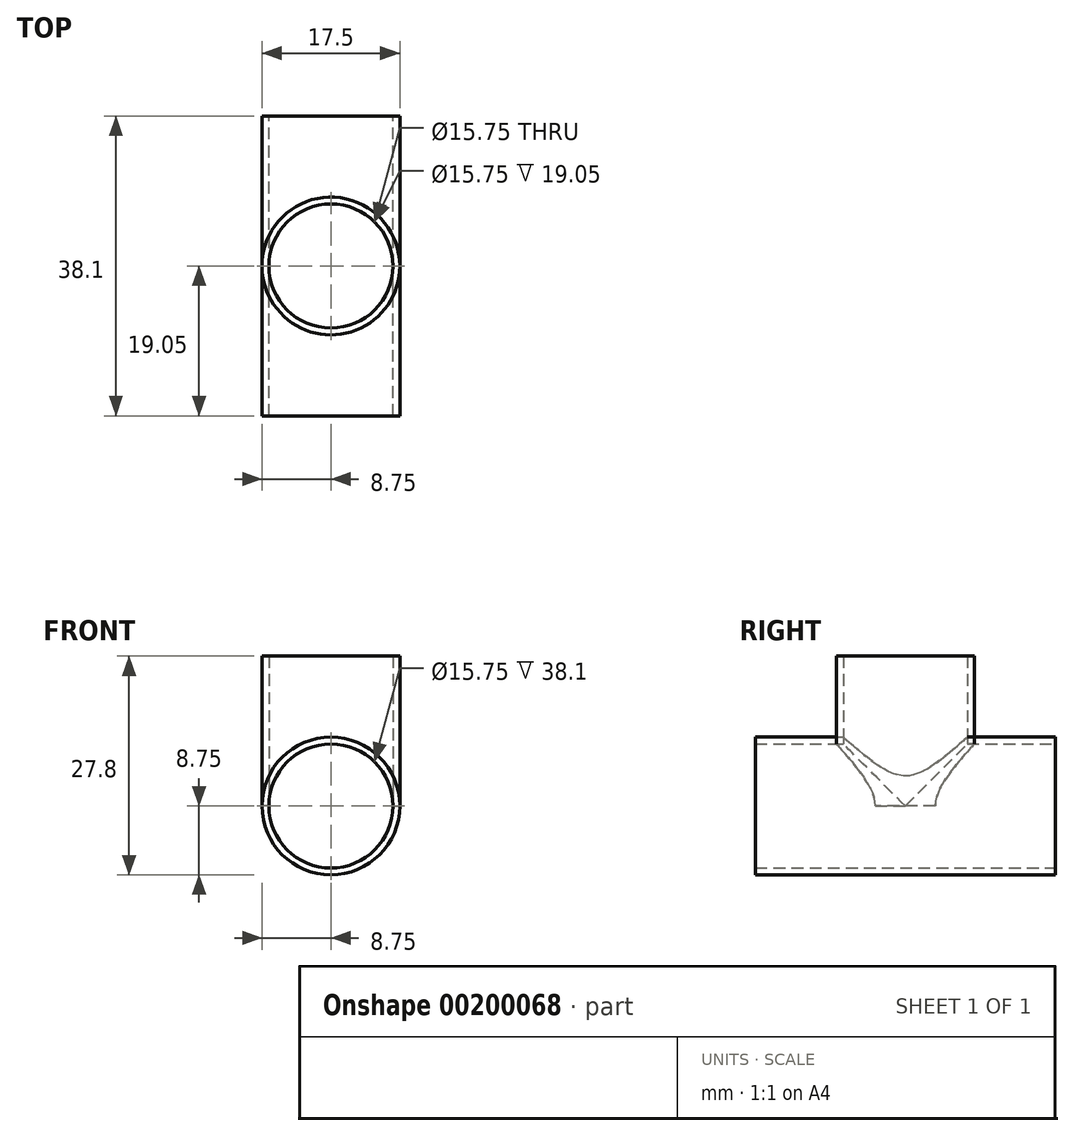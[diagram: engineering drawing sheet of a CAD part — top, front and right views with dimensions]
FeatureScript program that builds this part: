
annotation { "Feature Type Name" : "Feature", "Feature Type Description" : "" }
export const myFeature = defineFeature(function(context is Context, id is Id, definition is map)
    precondition{}
    {
        {
            var Q0;
            Q0=qCreatedBy(makeId("Front.planeOp"),FACE);
            var sketch = newSketch(context, id + "F0", { "sketchPlane" : qUnion([Q0])});
            skCircle(sketch, "E0", {"center": v(0, 0) * mm, "radius": 7.87 * mm});
            skCircle(sketch, "E1", {"center": v(0, 0) * mm, "radius": 8.75 * mm});
            skSolve(sketch);
        }
        {
            var Q0;
            Q0=qCreatedBy(makeId("Top.planeOp"),FACE);
            var sketch = newSketch(context, id + "F1", { "sketchPlane" : qUnion([Q0])});
            skCircle(sketch, "E2", {"center": v(0, 0) * mm, "radius": 8.75 * mm});
            skCircle(sketch, "E3", {"center": v(0, 0) * mm, "radius": 7.87 * mm});
            skSolve(sketch);
        }
        {
            var Q0;
            Q0=makeQuery(id+"F0.imprint","IMPRINT",FACE,{"disambiguationData":[TD([[makeQuery(id+"F0.imprint","IMPRINT",EDGE,{"derivedFrom":sQuery(id+"F0.wireOp",EDGE,"E0")}),-1.0]])]});
            extrude(context, id + "F2", {"entities" : qUnion([Q0]), "depth" : 19.05 * mm, "hasSecondDirection" : true, "secondDirectionOppositeDirection" : true, "secondDirectionDepth" : 19.05 * mm});
        }
        {
            var Q0;
            Q0=makeQuery(id+"F1.imprint","IMPRINT",FACE,{"disambiguationData":[TD([[makeQuery(id+"F1.imprint","IMPRINT",EDGE,{"derivedFrom":sQuery(id+"F1.wireOp",EDGE,"E2")}),1.0]])]});
            var Q1;
            Q1=sQuery(id+"F1.wireOp",EDGE,"E2");
            var Q2;
            Q2=sQuery(id+"F1.wireOp",EDGE,"E3");
            extrude(context, id + "F3", {"entities" : qUnion([Q0]), "surfaceEntities" : qUnion([Q1, Q2]), "depth" : 19.05 * mm});
        }
        {
            var Q0;
            Q0=sQuery(id+"F1.wireOp",VERTEX,"E3.center");
            var Q1;
            Q1=makeQuery(id+"F2.opExtrude","SWEPT_BODY",BODY,{"disambiguationData":[OSD([sQuery(id+"F0.wireOp",EDGE,"E0"),sQuery(id+"F0.wireOp",EDGE,"E1")])]});
            hole(context, id + "F4", {"style" : HoleStyle.SIMPLE, "endStyle" : HoleEndStyle.THROUGH, "oppositeDirection" : true, "holeDiameter" : 15.75 * mm, "locations" : qUnion([Q0]), "scope" : qUnion([Q1]), "isTappedThrough" : true});
        }
        {
            var Q0;
            Q0=sQuery(id+"F0.wireOp",VERTEX,"E0.center");
            var Q1;
            Q1=makeQuery(id+"F3.opExtrude","SWEPT_BODY",BODY,{"disambiguationData":[OSD([sQuery(id+"F1.wireOp",EDGE,"E2"),sQuery(id+"F1.wireOp",EDGE,"E3")])]});
            hole(context, id + "F5", {"style" : HoleStyle.SIMPLE, "endStyle" : HoleEndStyle.THROUGH, "oppositeDirection" : true, "holeDiameter" : 15.75 * mm, "startFromSketch" : true, "locations" : qUnion([Q0]), "scope" : qUnion([Q1]), "isTappedThrough" : true});
        }
        {
            var Q0;
            Q0=sQuery(id+"F0.wireOp",VERTEX,"E0.center");
            var Q1;
            Q1=makeQuery(id+"F3.opExtrude","SWEPT_BODY",BODY,{"disambiguationData":[OSD([sQuery(id+"F1.wireOp",EDGE,"E2"),sQuery(id+"F1.wireOp",EDGE,"E3")])]});
            hole(context, id + "F6", {"style" : HoleStyle.SIMPLE, "endStyle" : HoleEndStyle.THROUGH, "holeDiameter" : 15.75 * mm, "startFromSketch" : true, "locations" : qUnion([Q0]), "scope" : qUnion([Q1]), "isTappedThrough" : true});
        }
    });
